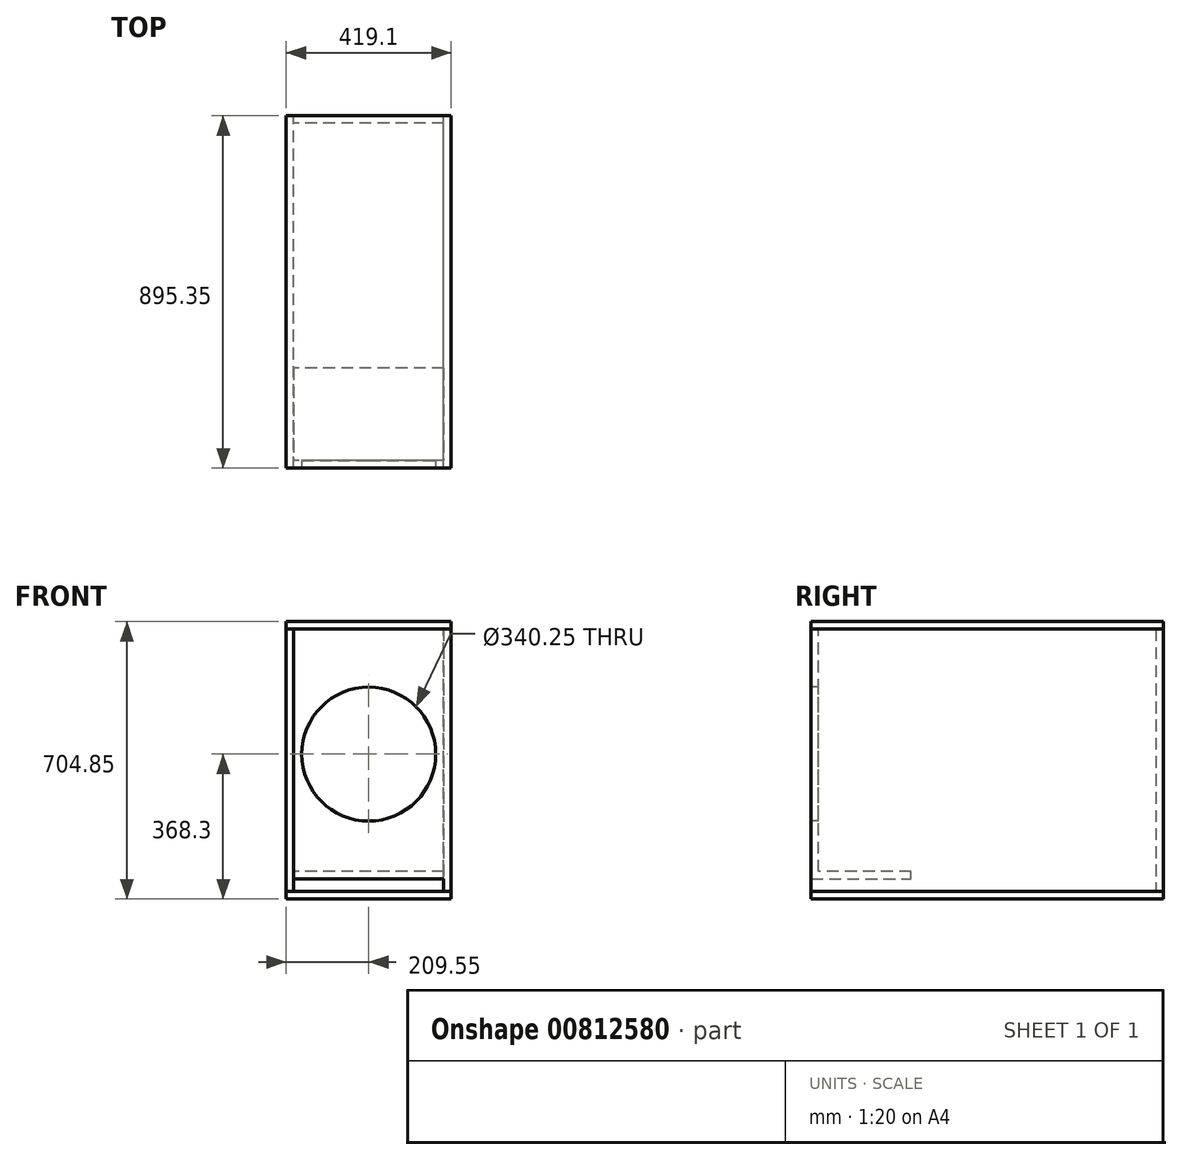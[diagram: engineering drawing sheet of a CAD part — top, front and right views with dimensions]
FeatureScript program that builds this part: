
annotation { "Feature Type Name" : "Feature", "Feature Type Description" : "" }
export const myFeature = defineFeature(function(context is Context, id is Id, definition is map)
    precondition{}
    {
        {
            var Q0;
            Q0=qCreatedBy(makeId("Front.planeOp"),FACE);
            var sketch = newSketch(context, id + "F0", { "sketchPlane" : qUnion([Q0])});
            skLineSegment(sketch, "E0.bottom", {"start": v(190.5, -317.5) * mm, "end": v(-190.5, -317.5) * mm});
            skLineSegment(sketch, "E0.top", {"start": v(190.5, 317.5) * mm, "end": v(-190.5, 317.5) * mm});
            skLineSegment(sketch, "E0.left", {"start": v(190.5, -317.5) * mm, "end": v(190.5, 317.5) * mm});
            skLineSegment(sketch, "E0.right", {"start": v(-190.5, -317.5) * mm, "end": v(-190.5, 317.5) * mm});
            skPoint(sketch, "E0.middle", {"position": v(0, 0) * mm});
            skSolve(sketch);
        }
        {
            var Q0;
            Q0 = qSketchRegion(id + "F0", true);
            extrude(context, id + "F1", {"entities" : qUnion([Q0]), "endBound" : BoundingType.SYMMETRIC, "depth" : 19.05 * mm, "offsetDistance" : 25.4 * mm});
        }
        {
            var Q0;
            Q0=makeQuery(id+"F1.opExtrude","CAP_FACE",FACE,{"disambiguationData":[OSD([sQuery(id+"F0.wireOp",EDGE,"E0.bottom"),sQuery(id+"F0.wireOp",EDGE,"E0.top"),sQuery(id+"F0.wireOp",EDGE,"E0.left"),sQuery(id+"F0.wireOp",EDGE,"E0.right")])],"isStart":false});
            var sketch = newSketch(context, id + "F2", { "sketchPlane" : qUnion([Q0])});
            skCircle(sketch, "E1", {"center": v(0, 0) * mm, "radius": 170.12 * mm});
            skSolve(sketch);
        }
        {
            var Q0;
            Q0 = qSketchRegion(id + "F2", true);
            extrude(context, id + "F3", {"entities" : qUnion([Q0]), "operationType" : NewBodyOperationType.REMOVE, "oppositeDirection" : true, "depth" : 19.05 * mm, "offsetDistance" : 25.4 * mm});
        }
        {
            var Q0;
            Q0=makeQuery(id+"F1.opExtrude","CAP_FACE",FACE,{"disambiguationData":[OSD([sQuery(id+"F0.wireOp",EDGE,"E0.bottom"),sQuery(id+"F0.wireOp",EDGE,"E0.top"),sQuery(id+"F0.wireOp",EDGE,"E0.left"),sQuery(id+"F0.wireOp",EDGE,"E0.right")])],"isStart":true});
            var sketch = newSketch(context, id + "F4", { "sketchPlane" : qUnion([Q0])});
            skLineSegment(sketch, "E2.bottom", {"start": v(-190.5, -317.5) * mm, "end": v(190.5, -317.5) * mm});
            skLineSegment(sketch, "E2.top", {"start": v(-190.5, -298.45) * mm, "end": v(190.5, -298.45) * mm});
            skLineSegment(sketch, "E2.left", {"start": v(-190.5, -317.5) * mm, "end": v(-190.5, -298.45) * mm});
            skLineSegment(sketch, "E2.right", {"start": v(190.5, -317.5) * mm, "end": v(190.5, -298.45) * mm});
            skSolve(sketch);
        }
        {
            var Q0;
            Q0 = qSketchRegion(id + "F4", true);
            extrude(context, id + "F5", {"entities" : qUnion([Q0]), "operationType" : NewBodyOperationType.ADD, "depth" : 234.95 * mm, "hasOffset" : true, "offsetDistance" : 234.95 * mm});
        }
        {
            var Q0;
            Q0=makeQuery(id+"F5.boolean.opBoolean","MERGE",FACE,{"derivedFrom":[makeQuery(id+"F1.opExtrude","SWEPT_FACE",FACE,{"disambiguationData":[OSD([sQuery(id+"F0.wireOp",EDGE,"E0.right")])]}),makeQuery(id+"F5.opExtrude","SWEPT_FACE",FACE,{"disambiguationData":[OSD([sQuery(id+"F4.wireOp",EDGE,"E2.right")])]})]});
            var sketch = newSketch(context, id + "F6", { "sketchPlane" : qUnion([Q0])});
            skLineSegment(sketch, "E3.bottom", {"start": v(9.53, 317.5) * mm, "end": v(-885.83, 317.5) * mm});
            skLineSegment(sketch, "E3.top", {"start": v(9.53, -349.25) * mm, "end": v(-885.82, -349.25) * mm});
            skLineSegment(sketch, "E3.left", {"start": v(9.53, 317.5) * mm, "end": v(9.53, -349.25) * mm});
            skLineSegment(sketch, "E3.right", {"start": v(-885.83, 317.5) * mm, "end": v(-885.83, -349.25) * mm});
            skSolve(sketch);
        }
        {
            var Q0;
            {var subQ0=sQuery(id+"F4.wireOp",EDGE,"E2.right");Q0=makeQuery(id+"F6.imprint","IMPRINT",FACE,{"disambiguationData":[TD([[makeQuery(id+"F6.imprint","IMPRINT",EDGE,{"derivedFrom":makeQuery(id+"F5.opExtrude","CAP_EDGE",EDGE,{"disambiguationData":[OSD([subQ0])],"isStart":false})}),-1.0]])]});}
            var Q1;
            {var subQ4=sQuery(id+"F6.wireOp",EDGE,"E3.top");Q1=makeQuery(id+"F6.imprint","IMPRINT",FACE,{"disambiguationData":[TD([[makeQuery(id+"F6.imprint","IMPRINT",EDGE,{"derivedFrom":subQ4}),-1.0]])]});}
            var Q2;
            Q2=sQuery(id+"F6.wireOp",EDGE,"E3.left");
            var Q3;
            Q3=sQuery(id+"F6.wireOp",EDGE,"E3.right");
            var Q4;
            Q4=sQuery(id+"F6.wireOp",EDGE,"E3.top");
            var Q5;
            Q5=sQuery(id+"F6.wireOp",EDGE,"E3.bottom");
            extrude(context, id + "F7", {"entities" : qUnion([Q0, Q1]), "surfaceOperationType" : NewSurfaceOperationType.ADD, "surfaceEntities" : qUnion([Q2, Q3, Q4, Q5]), "depth" : 19.05 * mm, "offsetDistance" : 25.4 * mm});
        }
        {
            var Q0;
            Q0=makeQuery(id+"F5.boolean.opBoolean","MERGE",FACE,{"derivedFrom":[makeQuery(id+"F1.opExtrude","SWEPT_FACE",FACE,{"disambiguationData":[OSD([sQuery(id+"F0.wireOp",EDGE,"E0.left")])]}),makeQuery(id+"F5.opExtrude","SWEPT_FACE",FACE,{"disambiguationData":[OSD([sQuery(id+"F4.wireOp",EDGE,"E2.left")])]})]});
            var sketch = newSketch(context, id + "F8", { "sketchPlane" : qUnion([Q0])});
            skLineSegment(sketch, "E4.bottom", {"start": v(-9.53, 317.5) * mm, "end": v(885.83, 317.5) * mm});
            skLineSegment(sketch, "E4.top", {"start": v(-9.52, -349.25) * mm, "end": v(885.83, -349.25) * mm});
            skLineSegment(sketch, "E4.left", {"start": v(-9.53, 317.5) * mm, "end": v(-9.53, -349.25) * mm});
            skLineSegment(sketch, "E4.right", {"start": v(885.83, 317.5) * mm, "end": v(885.83, -349.25) * mm});
            skSolve(sketch);
        }
        {
            var Q0;
            Q0 = qSketchRegion(id + "F8", true);
            extrude(context, id + "F9", {"entities" : qUnion([Q0]), "operationType" : NewBodyOperationType.ADD, "depth" : 19.05 * mm, "offsetDistance" : 25.4 * mm});
        }
        {
            var Q0;
            Q0=makeQuery(id+"F9.opExtrude","SWEPT_FACE",FACE,{"disambiguationData":[OSD([sQuery(id+"F8.wireOp",EDGE,"E4.top")])]});
            var sketch = newSketch(context, id + "F10", { "sketchPlane" : qUnion([Q0])});
            skLineSegment(sketch, "E5.bottom", {"start": v(209.55, 9.52) * mm, "end": v(-209.55, 9.52) * mm});
            skLineSegment(sketch, "E5.top", {"start": v(209.55, -885.83) * mm, "end": v(-209.55, -885.83) * mm});
            skLineSegment(sketch, "E5.left", {"start": v(209.55, 9.52) * mm, "end": v(209.55, -885.83) * mm});
            skLineSegment(sketch, "E5.right", {"start": v(-209.55, 9.52) * mm, "end": v(-209.55, -885.83) * mm});
            skSolve(sketch);
        }
        {
            var Q0;
            Q0 = qSketchRegion(id + "F10", true);
            extrude(context, id + "F11", {"entities" : qUnion([Q0]), "depth" : 19.05 * mm, "offsetDistance" : 25.4 * mm});
        }
        {
            var Q0;
            Q0=makeQuery(id+"F7.opExtrude","SWEPT_FACE",FACE,{"disambiguationData":[OSD([sQuery(id+"F6.wireOp",EDGE,"E3.bottom")])]});
            var sketch = newSketch(context, id + "F12", { "sketchPlane" : qUnion([Q0])});
            skLineSegment(sketch, "E6.bottom", {"start": v(-209.55, -9.53) * mm, "end": v(209.55, -9.53) * mm});
            skLineSegment(sketch, "E6.top", {"start": v(-209.55, 885.82) * mm, "end": v(209.55, 885.82) * mm});
            skLineSegment(sketch, "E6.left", {"start": v(-209.55, -9.53) * mm, "end": v(-209.55, 885.82) * mm});
            skLineSegment(sketch, "E6.right", {"start": v(209.55, -9.53) * mm, "end": v(209.55, 885.82) * mm});
            skSolve(sketch);
        }
        {
            var Q0;
            Q0 = qSketchRegion(id + "F12", true);
            extrude(context, id + "F13", {"entities" : qUnion([Q0]), "depth" : 19.05 * mm, "offsetDistance" : 25.4 * mm});
        }
        {
            var Q0;
            Q0=makeQuery(id+"F9.opExtrude","SWEPT_FACE",FACE,{"disambiguationData":[OSD([sQuery(id+"F8.wireOp",EDGE,"E4.right")])]});
            var sketch = newSketch(context, id + "F14", { "sketchPlane" : qUnion([Q0])});
            skLineSegment(sketch, "E7.bottom", {"start": v(-190.5, 317.5) * mm, "end": v(190.5, 317.5) * mm});
            skLineSegment(sketch, "E7.top", {"start": v(-190.5, -349.25) * mm, "end": v(190.5, -349.25) * mm});
            skLineSegment(sketch, "E7.left", {"start": v(-190.5, 317.5) * mm, "end": v(-190.5, -349.25) * mm});
            skLineSegment(sketch, "E7.right", {"start": v(190.5, 317.5) * mm, "end": v(190.5, -349.25) * mm});
            skSolve(sketch);
        }
        {
            var Q0;
            Q0 = qSketchRegion(id + "F14", true);
            extrude(context, id + "F15", {"entities" : qUnion([Q0]), "depth" : -19.05 * mm, "offsetDistance" : 25.4 * mm});
        }
    });
